# Revit family: VL2S-GFS150xSWxBQPx
name_source: partatom
category: Leuchten
units: mm (PartAtom-declared; Revit-internal decimal feet)

## family parameters
Basisbauteil = Fläche
Beim Laden mit Abzugskörper schneiden = Nein
Bemaßung runder Anschluss = Durchmesser verwenden
Gemeinsam genutzt = Nein
Lichtquelle = Ja
OmniClass-Nummer = 23.80.70.11
OmniClass-Titel = Luminaries for Internal Lighting
Raumberechnungspunkt = Nein
Teiletyp = Normal

## types (16) — shared parameters
Baugruppenkennzeichen = D5020200
Datei für fotometrisches Netz = VL2S-GFS_BQP.IES
Emissionsform beim Rendern sichtbar = Nein
Farbfilter = 16777215
Farbtemperaturverschiebung bei Dämpfen der Lampe = <Keine Auswahl>
Hersteller = RIDI Leuchten GmbH
Lampe = LED
Neigungswinkel = 90.00°
URL = www.ridi.de
Von Breite des Rechtecks ausssenden = 1477 mm  [stored 4.8458 ft]
Von Länge des Rechtecks aussenden = 85 mm  [stored 0.278871 ft]
brand = RIDI
conformity mark = CE
electrical safety class = 1
height = 77 mm  [stored 0.252625 ft]
ingress protection (IP) code = IP54
length = 1500 mm  [stored 4.92126 ft]
nominal frequency = 50-60Hz
nominal voltage = 230
voltage type (AC, DC, UC) = AC
width = 97 mm  [stored 0.318241 ft]
zero-valued in all types: Vorgabe-Ansicht

## per-type parameters (varying)
| type | Modell | Scheinlast | rated input power | weight |
| VL2S-GFS150-5FLSW840BQP0750 | 2550140SW | 53 VA | 53 | 2,9 kg |
| VL2S-GFS150-5FLSW840BQP1500 | 2550143SW | 103 VA | 103 | 3,3 kg |
| VL2S-GFS150-5FLSW830BQP0700 | 2550149SW | 53 VA | 53 | 2,9 kg |
| VL2S-GFS150-5FLSW830BQP1500 | 2550152SW | 103 VA | 103 | 3,3 kg |
| VL2S-GFS150-5FLSW850BQP0750 | 2550155SW | 53 VA | 53 | 2,9 kg |
| VL2S-GFS150-5FLSW850BQP1500 | 2550158SW | 103 VA | 103 | 3,3 kg |
| VL2S-GFS150-5FLSW865BQP0700 | 2550161SW | 53 VA | 53 | 2,9 kg |
| VL2S-GFS150-5FLSW865BQP1500 | 2550164SW | 103 VA | 103 | 3,3 kg |
| VL2S-GFS150-7DASW840BQP0750 | 2560140SW | 52 VA | 52 | 2,9 kg |
| VL2S-GFS150-7DASW840BQP1500 | 2560143SW | 102 VA | 102 | 3,3 kg |
| VL2S-GFS150-7DASW830BQP0700 | 2560149SW | 52 VA | 52 | 2,9 kg |
| VL2S-GFS150-7DASW830BQP1500 | 2560152SW | 102 VA | 102 | 3,3 kg |
| VL2S-GFS150-7DASW850BQP0750 | 2560155SW | 52 VA | 52 | 2,9 kg |
| VL2S-GFS150-7DASW850BQP1500 | 2560158SW | 102 VA | 102 | 3,3 kg |
| VL2S-GFS150-7DASW865BQP0700 | 2560161SW | 52 VA | 52 | 2,9 kg |
| VL2S-GFS150-7DASW865BQP1500 | 2560164SW | 102 VA | 102 | 3,3 kg |

note: column(s) folded — value = type name in every type: product name

note: [stored X ft] marks values corroborated as IEEE doubles in the binary element streams (Revit-internal decimal feet)
